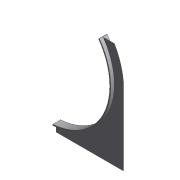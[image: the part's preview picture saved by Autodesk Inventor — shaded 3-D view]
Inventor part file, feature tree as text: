
AUTODESK INVENTOR PART (.ipt)
format: ipt  version: 2012 (Build 160160000, 160)  size: 108,032 bytes
history: native  units: in
note: dims shown in document units (in); Inventor stores cm internally (conversion verified against a paired STEP export)
features: extrude x2, sketch x2, fillet x1
ambient origin geometry x8: Origin, YZ Plane, XZ Plane, XY Plane, X Axis, Y Axis, Z Axis, Center Point
bodies: Solid1 (feature_tree)
feature tree (5):
  extrude  "Extrusion1"  Depth=0.3779in
  extrude  "Extrusion2"  Depth=0.625in TaperAngle=0.0deg
  fillet  "Fillet1"  Radius=1.75in
  sketch  "Sketch1"  dims[d4=11.0in d6=0.3779in]
  sketch  "Sketch2"  dims[d9=0.0625in d10=0.0in d12=0.625in d13=0.75in d14=0.0in d15=0.0in d17=1.75in d21=0.1875in d22=1.5in d23=1.0in]
